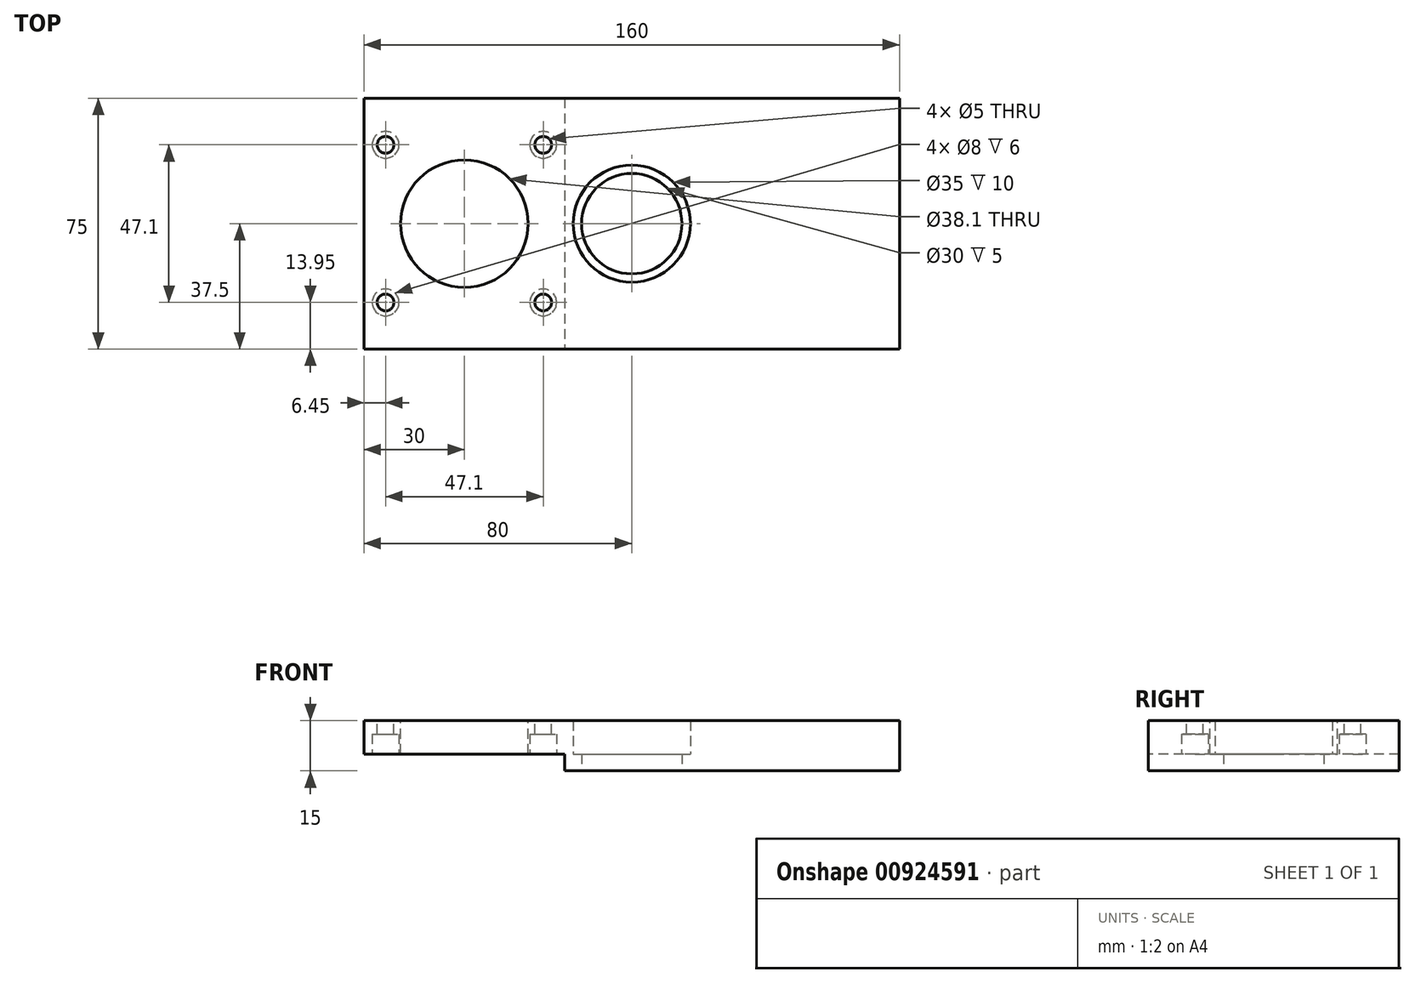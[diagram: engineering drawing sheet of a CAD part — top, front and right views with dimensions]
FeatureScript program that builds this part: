
annotation { "Feature Type Name" : "Feature", "Feature Type Description" : "" }
export const myFeature = defineFeature(function(context is Context, id is Id, definition is map)
    precondition{}
    {
        {
            var Q0;
            Q0=qCreatedBy(makeId("Top.planeOp"),FACE);
            var sketch = newSketch(context, id + "F0", { "sketchPlane" : qUnion([Q0])});
            skCircle(sketch, "E0", {"center": v(0, 0) * mm, "radius": 17.5 * mm});
            skLineSegment(sketch, "E1.bottom", {"start": v(80, -37.5) * mm, "end": v(-80, -37.5) * mm});
            skLineSegment(sketch, "E1.top", {"start": v(80, 37.5) * mm, "end": v(-80, 37.5) * mm});
            skLineSegment(sketch, "E1.left", {"start": v(80, -37.5) * mm, "end": v(80, 37.5) * mm});
            skLineSegment(sketch, "E1.right", {"start": v(-80, -37.5) * mm, "end": v(-80, 37.5) * mm});
            skSolve(sketch);
        }
        {
            var Q0;
            Q0=makeQuery(id+"F0.imprint","IMPRINT",FACE,{"disambiguationData":[TD([[makeQuery(id+"F0.imprint","IMPRINT",EDGE,{"derivedFrom":sQuery(id+"F0.wireOp",EDGE,"HPr2vzE0-l0NK-PHcw-MCR2-NGBl1DphhECB")}),1.0]])]});
            var Q1;
            Q1=makeQuery(id+"F0.imprint","IMPRINT",FACE,{"disambiguationData":[TD([[makeQuery(id+"F0.imprint","IMPRINT",EDGE,{"derivedFrom":sQuery(id+"F0.wireOp",EDGE,"E0")}),-1.0]])]});
            extrude(context, id + "F1", {"entities" : qUnion([Q0, Q1]), "depth" : 15 * mm, "offsetDistance" : 25 * mm});
        }
        {
            var Q0;
            Q0=makeQuery(id+"F1.opExtrude","CAP_FACE",FACE,{"disambiguationData":[OSD([sQuery(id+"F0.wireOp",EDGE,"E0"),sQuery(id+"F0.wireOp",EDGE,"E1.bottom"),sQuery(id+"F0.wireOp",EDGE,"E1.top"),sQuery(id+"F0.wireOp",EDGE,"E1.left"),sQuery(id+"F0.wireOp",EDGE,"E1.right")])],"isStart":false});
            var sketch = newSketch(context, id + "F2", { "sketchPlane" : qUnion([Q0])});
            skLineSegment(sketch, "E2.bottom", {"start": v(-26.45, -23.55) * mm, "end": v(-73.55, -23.55) * mm, "construction": true});
            skLineSegment(sketch, "E2.top", {"start": v(-26.45, 23.55) * mm, "end": v(-73.55, 23.55) * mm, "construction": true});
            skLineSegment(sketch, "E2.left", {"start": v(-26.45, -23.55) * mm, "end": v(-26.45, 23.55) * mm, "construction": true});
            skLineSegment(sketch, "E2.right", {"start": v(-73.55, -23.55) * mm, "end": v(-73.55, 23.55) * mm, "construction": true});
            skPoint(sketch, "E2.middle", {"position": v(-50, 0) * mm});
            skCircle(sketch, "E3", {"center": v(-73.55, 23.55) * mm, "radius": 2.5 * mm});
            skCircle(sketch, "E4", {"center": v(-26.45, 23.55) * mm, "radius": 2.5 * mm});
            skCircle(sketch, "E5", {"center": v(-26.45, -23.55) * mm, "radius": 2.5 * mm});
            skCircle(sketch, "E6", {"center": v(-73.55, -23.55) * mm, "radius": 2.5 * mm});
            skCircle(sketch, "E7", {"center": v(-50, 0) * mm, "radius": 19.05 * mm});
            skSolve(sketch);
        }
        {
            var Q0;
            Q0=qSketchRegion(id+"F2",true);
            extrude(context, id + "F3", {"entities" : qUnion([Q0]), "operationType" : NewBodyOperationType.REMOVE, "oppositeDirection" : true, "depth" : 25 * mm, "offsetDistance" : 25 * mm});
        }
        {
            var Q0;
            Q0=makeQuery(id+"F1.opExtrude","CAP_FACE",FACE,{"disambiguationData":[OSD([sQuery(id+"F0.wireOp",EDGE,"E0"),sQuery(id+"F0.wireOp",EDGE,"E1.bottom"),sQuery(id+"F0.wireOp",EDGE,"E1.top"),sQuery(id+"F0.wireOp",EDGE,"E1.left"),sQuery(id+"F0.wireOp",EDGE,"E1.right")])],"isStart":true});
            var sketch = newSketch(context, id + "F4", { "sketchPlane" : qUnion([Q0])});
            skCircle(sketch, "E8", {"center": v(-73.55, 23.55) * mm, "radius": 4 * mm});
            skCircle(sketch, "E9", {"center": v(-26.45, 23.55) * mm, "radius": 4 * mm});
            skCircle(sketch, "E10", {"center": v(-26.45, -23.55) * mm, "radius": 4 * mm});
            skCircle(sketch, "E11", {"center": v(-73.55, -23.55) * mm, "radius": 4 * mm});
            skSolve(sketch);
        }
        {
            var Q0;
            Q0=qSketchRegion(id+"F4",true);
            extrude(context, id + "F5", {"entities" : qUnion([Q0]), "operationType" : NewBodyOperationType.REMOVE, "oppositeDirection" : true, "depth" : 11 * mm, "offsetDistance" : 25 * mm});
        }
        {
            var Q0;
            Q0=makeQuery(id+"F1.opExtrude","SWEPT_FACE",FACE,{"disambiguationData":[OSD([sQuery(id+"F0.wireOp",EDGE,"E1.bottom")])]});
            var sketch = newSketch(context, id + "F6", { "sketchPlane" : qUnion([Q0])});
            skLineSegment(sketch, "E12.bottom", {"start": v(-20, 0) * mm, "end": v(-80, 0) * mm});
            skLineSegment(sketch, "E12.top", {"start": v(-20, 5) * mm, "end": v(-80, 5) * mm});
            skLineSegment(sketch, "E12.left", {"start": v(-20, 0) * mm, "end": v(-20, 5) * mm});
            skLineSegment(sketch, "E12.right", {"start": v(-80, 0) * mm, "end": v(-80, 5) * mm});
            skSolve(sketch);
        }
        {
            var Q0;
            Q0=makeQuery(id+"F6.imprint","IMPRINT",FACE,{"disambiguationData":[TD([[makeQuery(id+"F6.imprint","IMPRINT",EDGE,{"derivedFrom":sQuery(id+"F6.wireOp",EDGE,"E12.bottom")}),-1.0]])]});
            extrude(context, id + "F7", {"entities" : qUnion([Q0]), "operationType" : NewBodyOperationType.REMOVE, "oppositeDirection" : true, "depth" : 79.7 * mm, "offsetDistance" : 25 * mm});
        }
        {
            var Q0;
            Q0=makeQuery(id+"F1.opExtrude","CAP_FACE",FACE,{"disambiguationData":[OSD([sQuery(id+"F0.wireOp",EDGE,"E0"),sQuery(id+"F0.wireOp",EDGE,"E1.bottom"),sQuery(id+"F0.wireOp",EDGE,"E1.top"),sQuery(id+"F0.wireOp",EDGE,"E1.left"),sQuery(id+"F0.wireOp",EDGE,"E1.right")])],"isStart":true});
            var sketch = newSketch(context, id + "F8", { "sketchPlane" : qUnion([Q0])});
            skCircle(sketch, "E13", {"center": v(0, 0) * mm, "radius": 15 * mm});
            skCircle(sketch, "E14", {"center": v(0, 0) * mm, "radius": 19 * mm});
            skSolve(sketch);
        }
        {
            var Q0;
            Q0=makeQuery(id+"F8.imprint","IMPRINT",FACE,{"disambiguationData":[TD([[makeQuery(id+"F8.imprint","IMPRINT",EDGE,{"derivedFrom":sQuery(id+"F8.wireOp",EDGE,"E13")}),-1.0]])]});
            var Q1;
            Q1=makeQuery(id+"F8.imprint","IMPRINT",FACE,{"disambiguationData":[TD([[makeQuery(id+"F8.imprint","IMPRINT",EDGE,{"derivedFrom":sQuery(id+"F8.wireOp",EDGE,"E14")}),1.0]])]});
            extrude(context, id + "F9", {"entities" : qUnion([Q0, Q1]), "operationType" : NewBodyOperationType.ADD, "oppositeDirection" : true, "depth" : 5 * mm, "offsetDistance" : 25 * mm});
        }
    });
